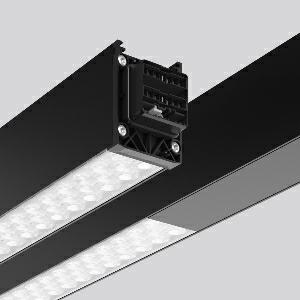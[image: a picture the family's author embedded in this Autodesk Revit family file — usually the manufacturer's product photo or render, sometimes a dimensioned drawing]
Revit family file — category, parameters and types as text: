
# Revit family: linedo_4_5m_90_10001000_954590_853_776_700_3d13
name_source: partatom
category: Lighting Fixtures
units: mm (PartAtom-declared; Revit-internal decimal feet)

## family parameters
Cut with Voids When Loaded = No
Host = Face
Light Source = No
Part Type = Normal
Room Calculation Point = No
Round Connector Dimension = Use Diameter
Shared = No

## types (1)
- LINEDO_4,5m_90_10001000 (1 x LED Modul 850, 1700 lm, 5000)
    Apparent Load = 21 VA
    CIE Flux Codes = 73 96 99 100 100
    Color Rendering = 80
    Color Temperature = 5000
    Default Elevation = 1800 mm
    Description = LINEDO, 21 W, 3400 lm, 850, black, DALI
Continuous line luminaire, L 4547 B 58 H 76
    Height = 76 mm
    Lamp = 1 x LED Modul 850
    Lamp Light Flux = 1700 lm
    Lamp count = 1
    Length = 4547 mm
    Lifetime = 50000 h
    Luminous efficacy = 162 lm/W
    Manufacturer = RZB
    ModVariant = No
    Model = 954590.853.776.700
    Mounting Place = Ceiling
    Mounting Type = Surface mounted, Pendant
    Number of Poles = 1
    OnlyDefault = Yes
    Power Factor = 1
    Product Name = LINEDO_4,5m_90_10001000
    Product group = Surface mounted continuous line luminaire system
    ProductGroupID = 310
    Protection Class = Protection class I
    Protection Degree = IP 54
    RLX_Detail_Level = 1
    RLX_Emergency_Light_Flux = 0 lm
    RLX_Emergency_Type = 0
    RLX_Emergency_Type_DB = No
    RlxData = <blob elided: 56809 chars, md5=21e307ad>
    Socket = socket
    Standby Power = 0 W
    System Light Flux = 3400 lm
    System Power = 21 W
    Type Comments = Product without accessories
    Type Image = 954590.853.476.504.jpg
    URL = http://relux.com
    VarID = ---
    Voltage = 230 V
    Voltage Range = 220-240 V
    Weight = 0.00 kg
    Width = 58 mm

## geometry (parser evidence)
native form markers: Blend x4, Sweep x13
no freeform markers — native parametric forms only
